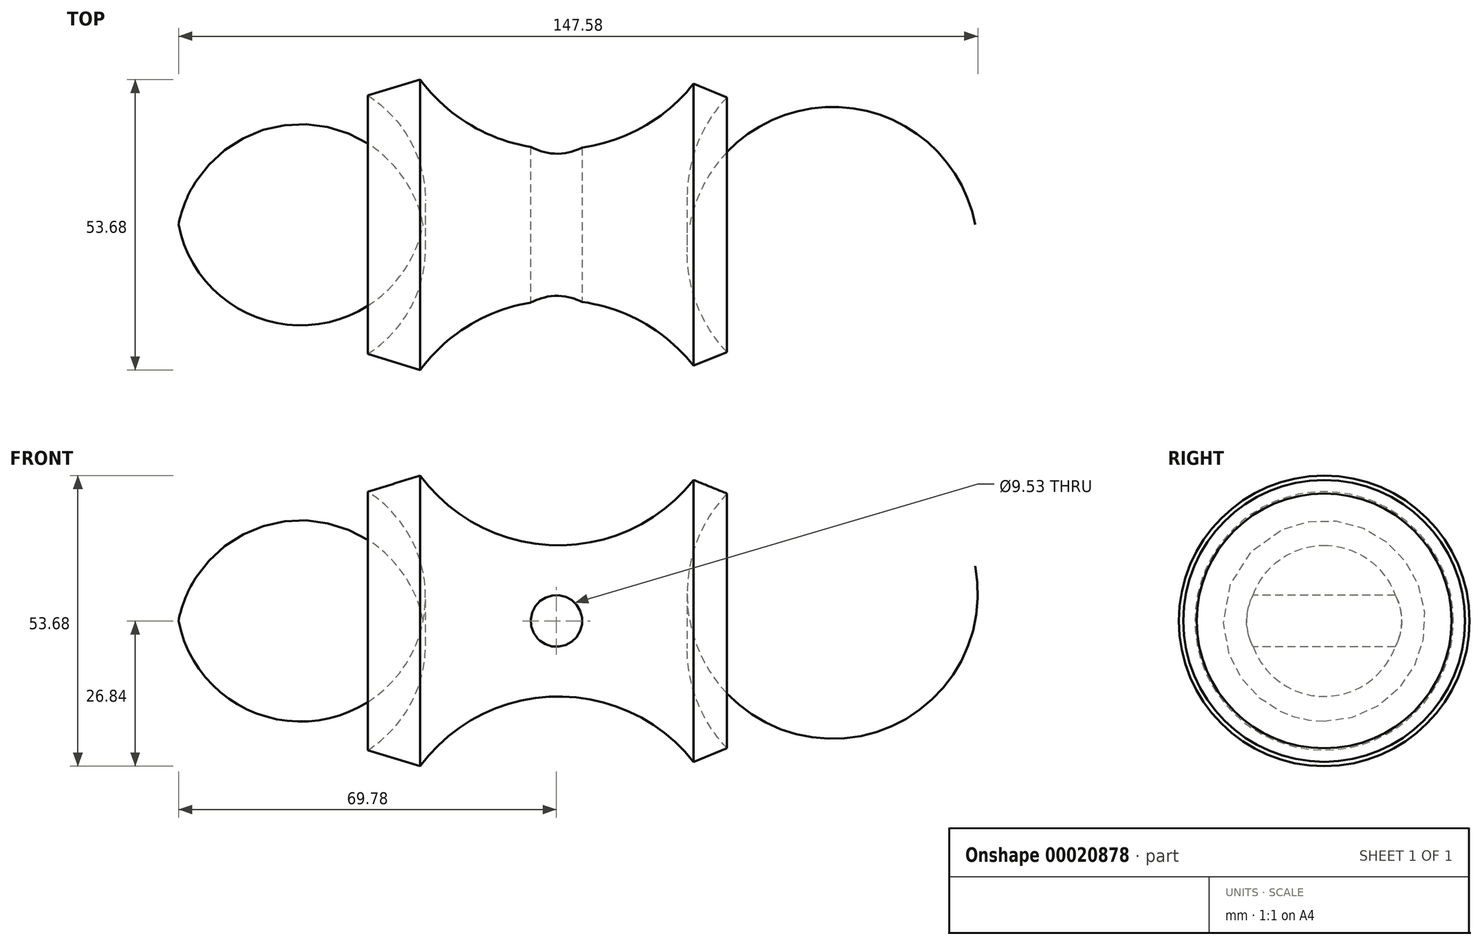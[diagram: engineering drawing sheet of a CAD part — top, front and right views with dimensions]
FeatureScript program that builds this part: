
annotation { "Feature Type Name" : "Feature", "Feature Type Description" : "" }
export const myFeature = defineFeature(function(context is Context, id is Id, definition is map)
    precondition{}
    {
        {
            var Q0;
            Q0=qCreatedBy(makeId("Front.planeOp"),FACE);
            var sketch = newSketch(context, id + "F0", { "sketchPlane" : qUnion([Q0])});
            skPoint(sketch, "E0.orphan", {"position": v(-11.12, 19.33) * mm});
            skArc(sketch, "E1", {"start": v(-24.6, 0) * mm, "mid": v(-26.04, 13.52) * mm, "end": v(-34.85, 23.86) * mm});
            skPoint(sketch, "E2", {"position": v(25.3, 26.03) * mm});
            skLineSegment(sketch, "E3", {"start": v(-34.85, 10.98) * mm, "end": v(0.07, 10.98) * mm, "construction": true});
            skLineSegment(sketch, "E4", {"start": v(-34.85, 23.86) * mm, "end": v(-25.16, 26.84) * mm});
            skLineSegment(sketch, "E5.MirrorCS", {"start": v(31.48, 23.53) * mm, "end": v(25.3, 26.03) * mm});
            skArc(sketch, "E6.MirrorCS", {"start": v(24.6, 0) * mm, "mid": v(25.2, 12.6) * mm, "end": v(31.48, 23.53) * mm});
            skArc(sketch, "E7", {"start": v(-25.16, 26.84) * mm, "mid": v(-0.12, 13.96) * mm, "end": v(25.3, 26.03) * mm});
            skPoint(sketch, "E8", {"position": v(-3.64, 4.48) * mm});
            skPoint(sketch, "E9.orphan", {"position": v(24.12, 5.07) * mm});
            skLineSegment(sketch, "E10", {"start": v(-24.6, 0) * mm, "end": v(24.6, 0) * mm});
            skPoint(sketch, "E11.orphan", {"position": v(-39.94, -17.41) * mm});
            skSolve(sketch);
        }
        {
            var Q0;
            Q0 = qSketchRegion(id + "F0", true);
            var Q1;
            Q1=sQuery(id+"F0.wireOp",EDGE,"E10");
            revolve(context, id + "F1", {"entities" : qUnion([Q0]), "axis" : qUnion([Q1]), "revolveType" : RevolveType.FULL});
        }
        {
            var Q0;
            Q0=qCreatedBy(makeId("Front.planeOp"),FACE);
            cPlane(context, id + "F2", {"entities" : qUnion([Q0]), "cplaneType" : CPlaneType.OFFSET, "offset" : 152.4 * mm, "width" : 152.4 * mm, "height" : 152.4 * mm});
        }
        {
            var Q0;
            Q0=qCreatedBy(id+"F2.planeOp",FACE);
            var sketch = newSketch(context, id + "F3", { "sketchPlane" : qUnion([Q0])});
            skCircle(sketch, "E12", {"center": v(0, 0) * mm, "radius": 4.76 * mm});
            skSolve(sketch);
        }
        {
            var Q0;
            Q0 = qSketchRegion(id + "F3", true);
            extrude(context, id + "F4", {"entities" : qUnion([Q0]), "operationType" : NewBodyOperationType.REMOVE, "endBound" : BoundingType.THROUGH_ALL, "oppositeDirection" : true, "depth" : 25.4 * mm});
        }
    });
